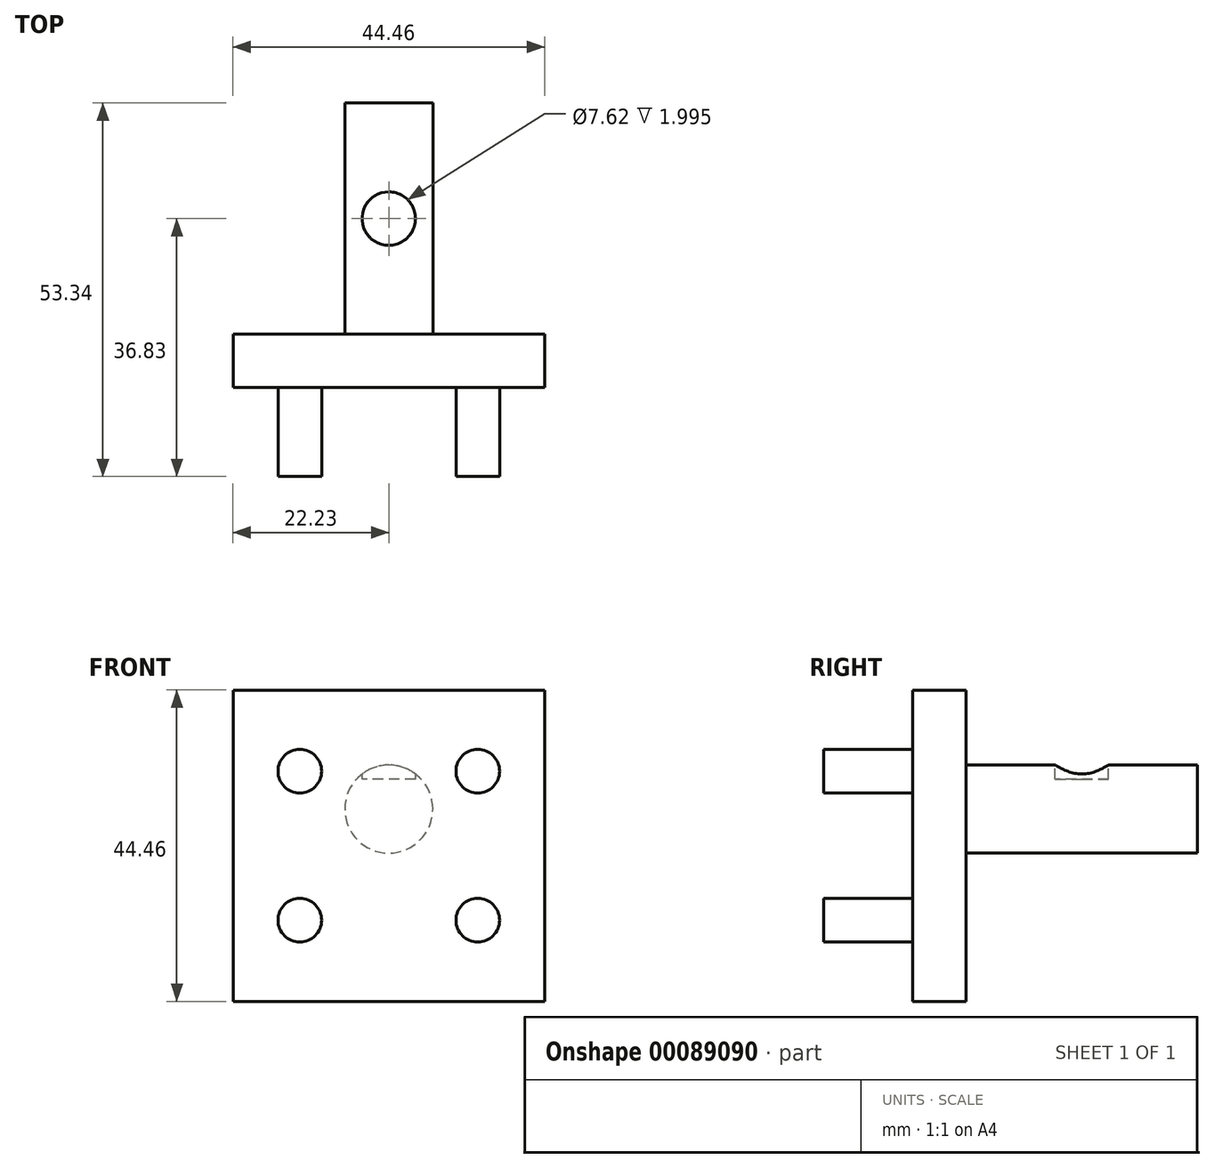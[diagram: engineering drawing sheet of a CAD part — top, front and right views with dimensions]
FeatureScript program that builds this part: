
annotation { "Feature Type Name" : "Feature", "Feature Type Description" : "" }
export const myFeature = defineFeature(function(context is Context, id is Id, definition is map)
    precondition{}
    {
        {
            var Q0;
            Q0=qCreatedBy(makeId("Front.planeOp"),FACE);
            var sketch = newSketch(context, id + "F0", { "sketchPlane" : qUnion([Q0])});
            skLineSegment(sketch, "E0.bottom", {"start": v(22.23, 22.23) * mm, "end": v(-22.23, 22.23) * mm});
            skLineSegment(sketch, "E0.top", {"start": v(22.23, -22.23) * mm, "end": v(-22.23, -22.23) * mm});
            skLineSegment(sketch, "E0.left", {"start": v(22.23, 22.23) * mm, "end": v(22.23, -22.23) * mm});
            skLineSegment(sketch, "E0.right", {"start": v(-22.23, 22.23) * mm, "end": v(-22.23, -22.23) * mm});
            skPoint(sketch, "E0.middle", {"position": v(0, 0) * mm});
            skSolve(sketch);
        }
        {
            var Q0;
            Q0 = qSketchRegion(id + "F0", true);
            extrude(context, id + "F1", {"entities" : qUnion([Q0]), "depth" : 7.62 * mm});
        }
        {
            var Q0;
            Q0=makeQuery(id+"F1.opExtrude","CAP_FACE",FACE,{"disambiguationData":[OSD([sQuery(id+"F0.wireOp",EDGE,"E0.bottom"),sQuery(id+"F0.wireOp",EDGE,"E0.top"),sQuery(id+"F0.wireOp",EDGE,"E0.left"),sQuery(id+"F0.wireOp",EDGE,"E0.right")])],"isStart":false});
            var sketch = newSketch(context, id + "F2", { "sketchPlane" : qUnion([Q0])});
            skCircle(sketch, "E1", {"center": v(-12.7, 10.64) * mm, "radius": 3.11 * mm});
            skCircle(sketch, "E2", {"center": v(12.7, 10.64) * mm, "radius": 3.11 * mm});
            skLineSegment(sketch, "E3", {"start": v(0, 22.23) * mm, "end": v(0, -22.23) * mm, "construction": true});
            skCircle(sketch, "E4.MirrorC", {"center": v(12.7, -10.64) * mm, "radius": 3.11 * mm});
            skCircle(sketch, "E5.MirrorC", {"center": v(-12.7, -10.64) * mm, "radius": 3.11 * mm});
            skSolve(sketch);
        }
        {
            var Q0;
            Q0 = qSketchRegion(id + "F2", true);
            extrude(context, id + "F3", {"entities" : qUnion([Q0]), "operationType" : NewBodyOperationType.ADD, "depth" : 12.7 * mm});
        }
        {
            var Q0;
            Q0=makeQuery(id+"F1.opExtrude","CAP_FACE",FACE,{"disambiguationData":[OSD([sQuery(id+"F0.wireOp",EDGE,"E0.bottom"),sQuery(id+"F0.wireOp",EDGE,"E0.top"),sQuery(id+"F0.wireOp",EDGE,"E0.left"),sQuery(id+"F0.wireOp",EDGE,"E0.right")])],"isStart":true});
            var sketch = newSketch(context, id + "F4", { "sketchPlane" : qUnion([Q0])});
            skCircle(sketch, "E6", {"center": v(0, 5.23) * mm, "radius": 6.29 * mm});
            skSolve(sketch);
        }
        {
            var Q0;
            Q0 = qSketchRegion(id + "F4", true);
            extrude(context, id + "F5", {"entities" : qUnion([Q0]), "operationType" : NewBodyOperationType.ADD, "depth" : 33.02 * mm});
        }
        {
            var Q0;
            Q0=makeQuery(id+"F1.opExtrude","SWEPT_FACE",FACE,{"disambiguationData":[OSD([sQuery(id+"F0.wireOp",EDGE,"E0.bottom")])]});
            var sketch = newSketch(context, id + "F6", { "sketchPlane" : qUnion([Q0])});
            skCircle(sketch, "E7", {"center": v(0, 16.51) * mm, "radius": 3.8 * mm});
            skSolve(sketch);
        }
        {
            var Q0;
            Q0 = qSketchRegion(id + "F6", true);
            extrude(context, id + "F7", {"entities" : qUnion([Q0]), "operationType" : NewBodyOperationType.REMOVE, "oppositeDirection" : true, "depth" : 12.7 * mm});
        }
    });
